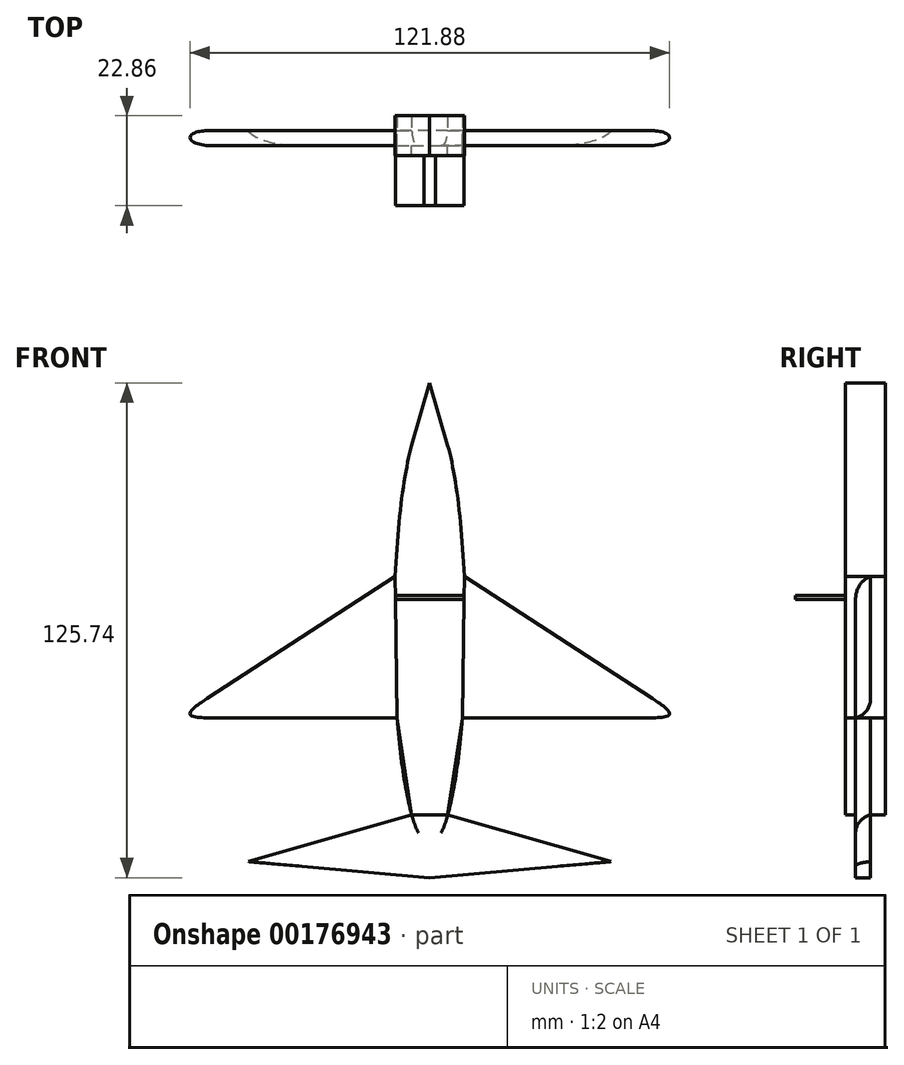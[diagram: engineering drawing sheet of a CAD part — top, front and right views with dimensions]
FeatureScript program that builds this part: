
annotation { "Feature Type Name" : "Feature", "Feature Type Description" : "" }
export const myFeature = defineFeature(function(context is Context, id is Id, definition is map)
    precondition{}
    {
        {
            var Q0;
            Q0=qCreatedBy(makeId("Front.planeOp"),FACE);
            var sketch = newSketch(context, id + "F0", { "sketchPlane" : qUnion([Q0])});
            skEllipse(sketch, "E0", {"center": v(0, 0) * mm, "majorRadius": 54.3 * mm, "minorRadius": 9.06 * mm, "majorAxis": v(0, 1)});
            skLineSegment(sketch, "E1", {"start": v(-8.77, 13.65) * mm, "end": v(-64.14, -22.26) * mm});
            skLineSegment(sketch, "E2", {"start": v(-64.14, -22.26) * mm, "end": v(-8.26, -22.26) * mm});
            skLineSegment(sketch, "E3", {"start": v(-8.26, -22.26) * mm, "end": v(8.26, -22.26) * mm});
            skLineSegment(sketch, "E4", {"start": v(8.26, -22.26) * mm, "end": v(64.14, -22.26) * mm});
            skLineSegment(sketch, "E5", {"start": v(-8.77, 13.65) * mm, "end": v(8.77, 13.65) * mm});
            skLineSegment(sketch, "E6", {"start": v(8.77, 13.65) * mm, "end": v(64.14, -22.26) * mm});
            skLineSegment(sketch, "E7", {"start": v(-4.57, -46.9) * mm, "end": v(4.57, -46.9) * mm});
            skLineSegment(sketch, "E8", {"start": v(4.57, -46.9) * mm, "end": v(0, -62.87) * mm});
            skLineSegment(sketch, "E9", {"start": v(0, -62.87) * mm, "end": v(-4.57, -46.9) * mm});
            skLineSegment(sketch, "E10", {"start": v(-4.57, 46.9) * mm, "end": v(4.57, 46.9) * mm});
            skLineSegment(sketch, "E11", {"start": v(4.57, 46.9) * mm, "end": v(0, 62.87) * mm});
            skLineSegment(sketch, "E12", {"start": v(0, 62.87) * mm, "end": v(-4.57, 46.9) * mm});
            skLineSegment(sketch, "E13", {"start": v(-4.57, -46.9) * mm, "end": v(-46.08, -58.77) * mm});
            skLineSegment(sketch, "E14", {"start": v(-46.08, -58.77) * mm, "end": v(0, -62.87) * mm});
            skLineSegment(sketch, "E15", {"start": v(4.57, -46.9) * mm, "end": v(46.08, -58.77) * mm});
            skLineSegment(sketch, "E16", {"start": v(46.08, -58.77) * mm, "end": v(0, -62.87) * mm});
            skSolve(sketch);
        }
        {
            var Q0;
            Q0 = qSketchRegion(id + "F0", true);
            extrude(context, id + "F1", {"entities" : qUnion([Q0]), "depth" : 3.8 * mm});
        }
        {
            var Q0;
            Q0=makeQuery(id+"F1.opExtrude","CAP_FACE",FACE,{"disambiguationData":[OSD([sQuery(id+"F0.wireOp",EDGE,"E0"),sQuery(id+"F0.wireOp",EDGE,"E1"),sQuery(id+"F0.wireOp",EDGE,"E2"),sQuery(id+"F0.wireOp",EDGE,"E4"),sQuery(id+"F0.wireOp",EDGE,"E6"),sQuery(id+"F0.wireOp",EDGE,"E11"),sQuery(id+"F0.wireOp",EDGE,"E12"),sQuery(id+"F0.wireOp",EDGE,"E13"),sQuery(id+"F0.wireOp",EDGE,"E14"),sQuery(id+"F0.wireOp",EDGE,"E15"),sQuery(id+"F0.wireOp",EDGE,"E16")])],"isStart":false});
            var sketch = newSketch(context, id + "F2", { "sketchPlane" : qUnion([Q0])});
            skLineSegment(sketch, "E17", {"start": v(-8.77, 13.65) * mm, "end": v(-8.26, -22.26) * mm});
            skLineSegment(sketch, "E18", {"start": v(-8.26, -22.26) * mm, "end": v(-4.57, -46.9) * mm});
            skLineSegment(sketch, "E19", {"start": v(-4.57, -46.9) * mm, "end": v(4.57, -46.9) * mm});
            skLineSegment(sketch, "E20", {"start": v(4.57, -46.9) * mm, "end": v(8.26, -22.26) * mm});
            skLineSegment(sketch, "E21", {"start": v(8.26, -22.26) * mm, "end": v(8.77, 13.65) * mm});
            skSolve(sketch);
        }
        {
            var Q0;
            Q0 = qSketchRegion(id + "F2", true);
            var Q1;
            Q1=makeQuery(id+"F2.imprint","IMPRINT",FACE,{"disambiguationData":[TD([[makeQuery(id+"F2.imprint","IMPRINT",EDGE,{"derivedFrom":sQuery(id+"F2.wireOp",EDGE,"E17")}),1.0]])]});
            extrude(context, id + "F3", {"entities" : qUnion([Q0, Q1]), "operationType" : NewBodyOperationType.ADD, "depth" : 2.54 * mm});
        }
        {
            var Q0;
            Q0=makeQuery(id+"F1.opExtrude","CAP_FACE",FACE,{"disambiguationData":[OSD([sQuery(id+"F0.wireOp",EDGE,"E0"),sQuery(id+"F0.wireOp",EDGE,"E1"),sQuery(id+"F0.wireOp",EDGE,"E2"),sQuery(id+"F0.wireOp",EDGE,"E4"),sQuery(id+"F0.wireOp",EDGE,"E6"),sQuery(id+"F0.wireOp",EDGE,"E11"),sQuery(id+"F0.wireOp",EDGE,"E12"),sQuery(id+"F0.wireOp",EDGE,"E13"),sQuery(id+"F0.wireOp",EDGE,"E14"),sQuery(id+"F0.wireOp",EDGE,"E15"),sQuery(id+"F0.wireOp",EDGE,"E16")])],"isStart":true});
            var sketch = newSketch(context, id + "F4", { "sketchPlane" : qUnion([Q0])});
            skLineSegment(sketch, "E22", {"start": v(-8.77, 13.65) * mm, "end": v(-8.26, -22.26) * mm});
            skLineSegment(sketch, "E23", {"start": v(-8.26, -22.26) * mm, "end": v(-4.57, -46.9) * mm});
            skLineSegment(sketch, "E24", {"start": v(-4.57, -46.9) * mm, "end": v(4.57, -46.9) * mm});
            skLineSegment(sketch, "E25", {"start": v(4.57, -46.9) * mm, "end": v(8.26, -22.26) * mm});
            skLineSegment(sketch, "E26", {"start": v(8.26, -22.26) * mm, "end": v(8.77, 13.65) * mm});
            skSolve(sketch);
        }
        {
            var Q0;
            Q0 = qSketchRegion(id + "F4", true);
            var Q1;
            Q1=makeQuery(id+"F4.imprint","IMPRINT",FACE,{"disambiguationData":[TD([[makeQuery(id+"F4.imprint","IMPRINT",EDGE,{"derivedFrom":sQuery(id+"F4.wireOp",EDGE,"E22")}),1.0]])]});
            extrude(context, id + "F5", {"entities" : qUnion([Q0, Q1]), "operationType" : NewBodyOperationType.ADD, "depth" : 3.8 * mm});
        }
        {
            var Q0;
            Q0=makeQuery(id+"F1.opExtrude","CAP_EDGE",EDGE,{"disambiguationData":[OSD([sQuery(id+"F0.wireOp",EDGE,"E1")])],"isStart":false});
            var Q1;
            Q1=makeQuery(id+"F1.opExtrude","CAP_EDGE",EDGE,{"disambiguationData":[OSD([sQuery(id+"F0.wireOp",EDGE,"E6")])],"isStart":false});
            var Q2;
            Q2=makeQuery(id+"F1.opExtrude","CAP_EDGE",EDGE,{"disambiguationData":[OSD([sQuery(id+"F0.wireOp",EDGE,"E13")])],"isStart":false});
            var Q3;
            Q3=makeQuery(id+"F1.opExtrude","CAP_EDGE",EDGE,{"disambiguationData":[OSD([sQuery(id+"F0.wireOp",EDGE,"E15")])],"isStart":false});
            fillet(context, id + "F6", {"entities" : qUnion([Q0, Q1, Q2, Q3]), "radius" : 5.08 * mm, "tangentPropagation" : true, "allowEdgeOverflow" : false});
        }
        {
            var Q0;
            Q0=makeQuery(id+"F1.opExtrude","CAP_EDGE",EDGE,{"disambiguationData":[OSD([sQuery(id+"F0.wireOp",EDGE,"E4")])],"isStart":true});
            var Q1;
            Q1=makeQuery(id+"F1.opExtrude","CAP_EDGE",EDGE,{"disambiguationData":[OSD([sQuery(id+"F0.wireOp",EDGE,"E2")])],"isStart":true});
            fillet(context, id + "F7", {"entities" : qUnion([Q0, Q1]), "radius" : 5.08 * mm, "tangentPropagation" : true, "allowEdgeOverflow" : false});
        }
        {
            var Q0;
            Q0=makeQuery(id+"F3.opExtrude","CAP_FACE",FACE,{"disambiguationData":[OSD([sQuery(id+"F0.wireOp",EDGE,"E0"),sQuery(id+"F0.wireOp",EDGE,"E11"),sQuery(id+"F0.wireOp",EDGE,"E12"),sQuery(id+"F2.wireOp",EDGE,"E17"),sQuery(id+"F2.wireOp",EDGE,"E18"),sQuery(id+"F2.wireOp",EDGE,"E19"),sQuery(id+"F2.wireOp",EDGE,"E20"),sQuery(id+"F2.wireOp",EDGE,"E21")])],"isStart":false});
            var sketch = newSketch(context, id + "F8", { "sketchPlane" : qUnion([Q0])});
            skLineSegment(sketch, "E27", {"start": v(-8.69, 7.82) * mm, "end": v(8.69, 7.82) * mm});
            skLineSegment(sketch, "E28.bottom", {"start": v(-8.69, 7.82) * mm, "end": v(-1.5, 7.82) * mm});
            skLineSegment(sketch, "E28.top", {"start": v(-8.69, 8.9) * mm, "end": v(-1.5, 8.9) * mm});
            skLineSegment(sketch, "E28.left", {"start": v(-8.69, 7.82) * mm, "end": v(-8.69, 8.9) * mm});
            skLineSegment(sketch, "E28.right", {"start": v(-1.5, 7.82) * mm, "end": v(-1.5, 8.9) * mm});
            skLineSegment(sketch, "E29.bottom", {"start": v(8.69, 7.82) * mm, "end": v(1.4, 7.82) * mm});
            skLineSegment(sketch, "E29.top", {"start": v(8.69, 8.83) * mm, "end": v(1.4, 8.83) * mm});
            skLineSegment(sketch, "E29.left", {"start": v(8.69, 7.82) * mm, "end": v(8.69, 8.83) * mm});
            skLineSegment(sketch, "E29.right", {"start": v(1.4, 7.82) * mm, "end": v(1.4, 8.83) * mm});
            skLineSegment(sketch, "E30", {"start": v(-1.5, 8.9) * mm, "end": v(1.4, 8.83) * mm});
            skSolve(sketch);
        }
        {
            var Q0;
            Q0 = qSketchRegion(id + "F8", true);
            extrude(context, id + "F9", {"entities" : qUnion([Q0]), "operationType" : NewBodyOperationType.ADD, "depth" : 12.7 * mm});
        }
        {
            var Q0;
            Q0 = qSketchRegion(id + "F8", true);
            extrude(context, id + "F10", {"entities" : qUnion([Q0]), "operationType" : NewBodyOperationType.ADD, "depth" : 5.08 * mm});
        }
    });
